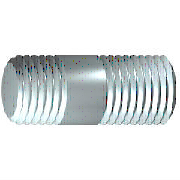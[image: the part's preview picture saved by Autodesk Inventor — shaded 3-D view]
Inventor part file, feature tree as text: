
AUTODESK INVENTOR PART (.ipt)
format: ipt  version: 2017 (Build 210142000, 142)  size: 146,432 bytes
history: native  units: mm (DEFAULTED — no unit token found)
features: sketch x1
ambient origin geometry x8: Origin, YZ Plane, XZ Plane, XY Plane, X Axis, Y Axis, Z Axis, Center Point
bodies: Solid1 (feature_tree), Body (feature_tree)
feature tree (1):
  sketch  "Sketch1"  dims[d0=3.0mm d3=90.0deg d1=3.0mm d2=0.0mm d4=3.0mm d5=20.0mm d6=12.0mm d7=12.306725mm d8=0.0mm d9=0.307725mm d10=0.306725mm d11=0.501mm d12=0.306725mm d13=3.0mm d69=45.0deg d70=45.0deg d78=0.0mm d80=-12.306725mm d86=-2.5mm]
